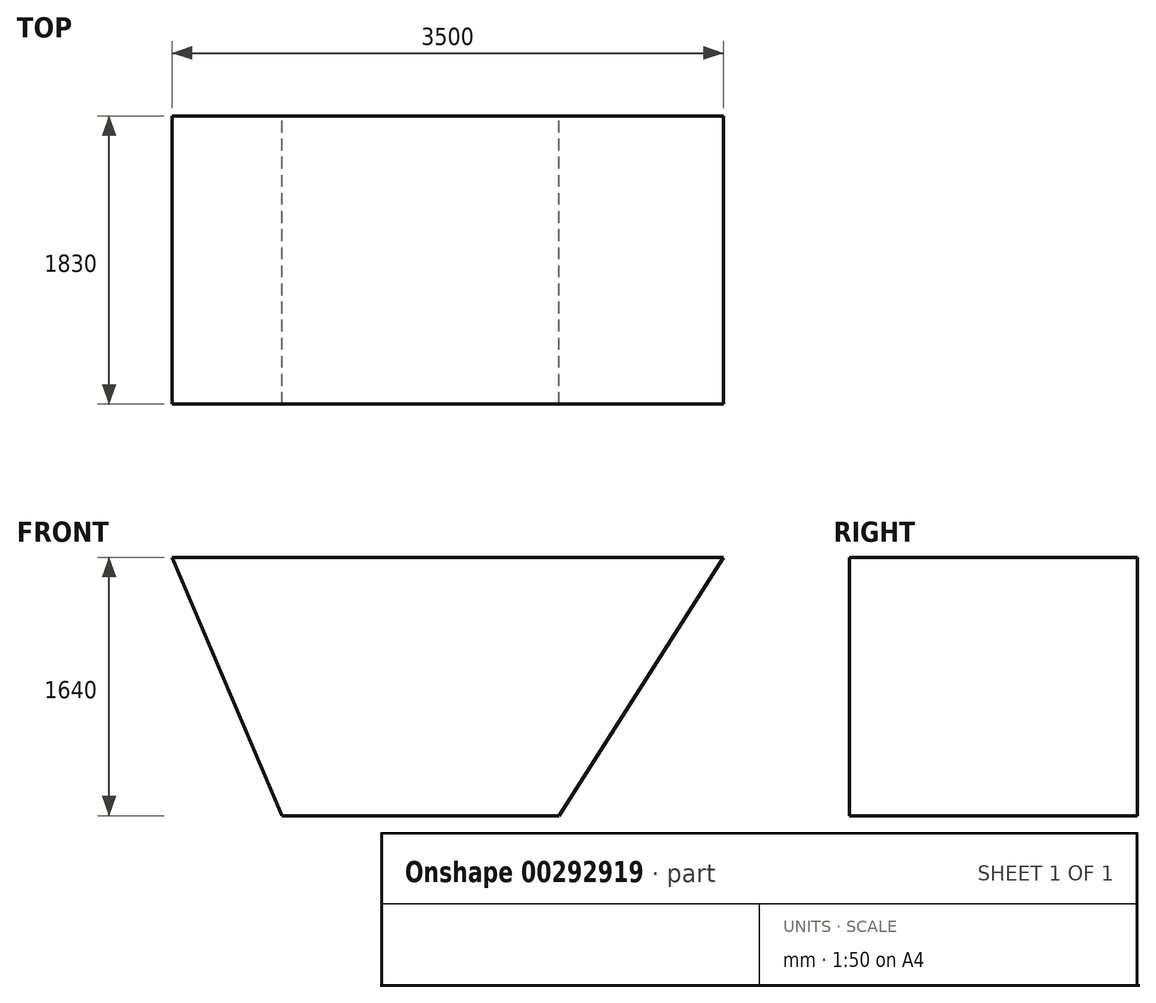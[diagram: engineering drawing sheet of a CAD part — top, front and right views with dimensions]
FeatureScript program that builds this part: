
annotation { "Feature Type Name" : "Feature", "Feature Type Description" : "" }
export const myFeature = defineFeature(function(context is Context, id is Id, definition is map)
    precondition{}
    {
        {
            var Q0;
            Q0=qCreatedBy(makeId("Front.planeOp"),FACE);
            var sketch = newSketch(context, id + "F0", { "sketchPlane" : qUnion([Q0])});
            skLineSegment(sketch, "E0", {"start": v(-1794.7, 1640) * mm, "end": v(1705.3, 1640) * mm});
            skLineSegment(sketch, "E1", {"start": v(0, 0) * mm, "end": v(663.05, 0) * mm});
            skLineSegment(sketch, "E2", {"start": v(0, 0) * mm, "end": v(-1096.95, 0) * mm});
            skLineSegment(sketch, "E3", {"start": v(-1794.7, 1640) * mm, "end": v(-1096.95, 0) * mm});
            skLineSegment(sketch, "E4", {"start": v(1705.3, 1640) * mm, "end": v(663.05, 0) * mm});
            skSolve(sketch);
        }
        {
            var Q0;
            Q0 = qSketchRegion(id + "F0", true);
            extrude(context, id + "F1", {"entities" : qUnion([Q0]), "depth" : 1830 * mm});
        }
    });
